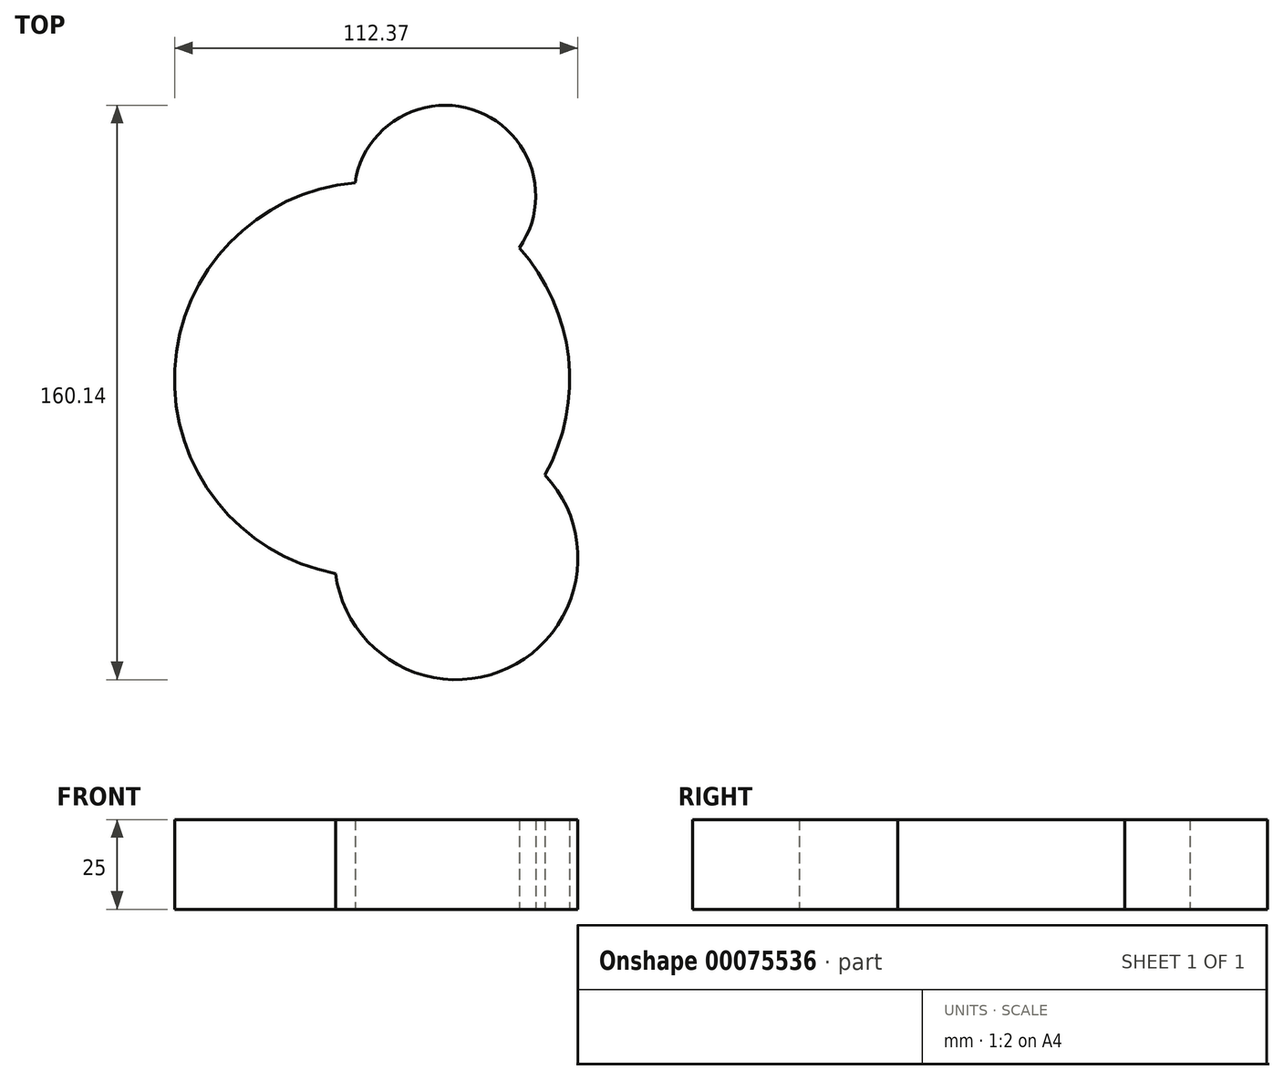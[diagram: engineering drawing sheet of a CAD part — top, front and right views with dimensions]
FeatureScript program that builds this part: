
annotation { "Feature Type Name" : "Feature", "Feature Type Description" : "" }
export const myFeature = defineFeature(function(context is Context, id is Id, definition is map)
    precondition{}
    {
        {
            var Q0;
            Q0=qCreatedBy(makeId("Top.planeOp"),FACE);
            var sketch = newSketch(context, id + "F0", { "sketchPlane" : qUnion([Q0])});
            skArc(sketch, "E0", {"start": v(48.17, -26.63) * mm, "mid": v(54.69, 6.17) * mm, "end": v(41.02, 36.7) * mm});
            skArc(sketch, "E1", {"start": v(-10.19, -54.09) * mm, "mid": v(37.86, -80.47) * mm, "end": v(48.17, -26.63) * mm});
            skArc(sketch, "E2", {"start": v(41.02, 36.7) * mm, "mid": v(29.6, 74.67) * mm, "end": v(-4.74, 54.83) * mm});
            skArc(sketch, "E3.trimOffspring", {"start": v(-4.74, 54.83) * mm, "mid": v(-54.97, 2.75) * mm, "end": v(-10.19, -54.09) * mm});
            skSolve(sketch);
        }
        {
            var Q0;
            Q0=makeQuery(id+"F0.imprint","IMPRINT",FACE,{"disambiguationData":[TD([[makeQuery(id+"F0.imprint","IMPRINT",EDGE,{"derivedFrom":sQuery(id+"F0.wireOp",EDGE,"E0")}),1.0]])]});
            extrude(context, id + "F1", {"entities" : qUnion([Q0]), "endBound" : BoundingType.SYMMETRIC, "depth" : 25 * mm});
        }
    });
